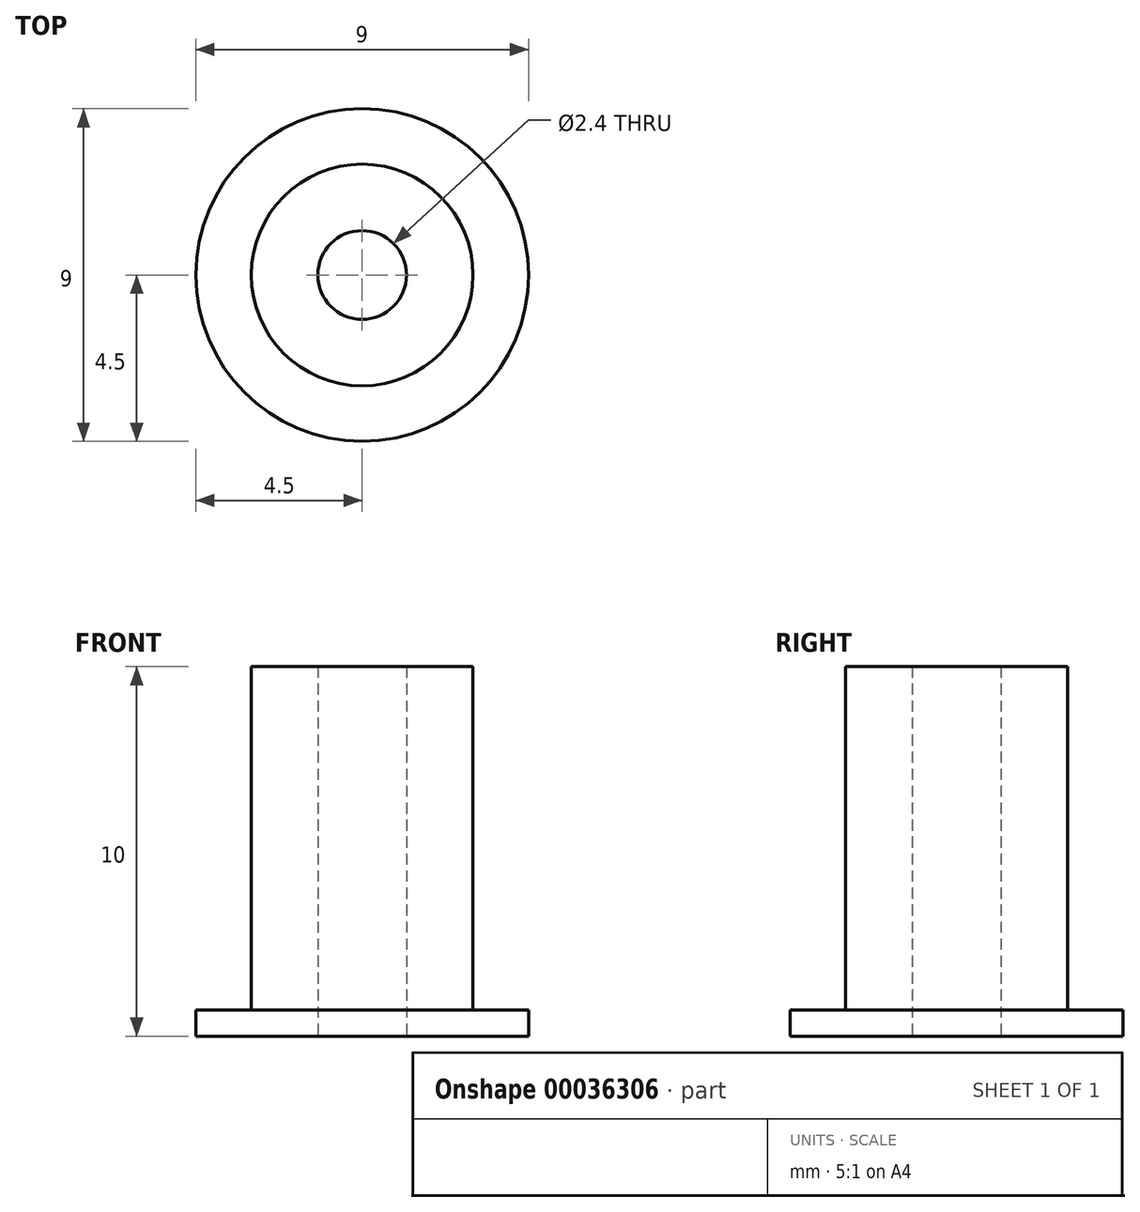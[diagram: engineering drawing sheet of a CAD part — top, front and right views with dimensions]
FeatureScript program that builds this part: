
annotation { "Feature Type Name" : "Feature", "Feature Type Description" : "" }
export const myFeature = defineFeature(function(context is Context, id is Id, definition is map)
    precondition{}
    {
        {
            var Q0;
            Q0=qCreatedBy(makeId("Top.planeOp"),FACE);
            var sketch = newSketch(context, id + "F0", { "sketchPlane" : qUnion([Q0])});
            skCircle(sketch, "E0", {"center": v(0, 0) * mm, "radius": 3 * mm});
            skCircle(sketch, "E1", {"center": v(0, 0) * mm, "radius": 4.5 * mm});
            skCircle(sketch, "E2", {"center": v(0, 0) * mm, "radius": 1.2 * mm});
            skSolve(sketch);
        }
        {
            var Q0;
            Q0=makeQuery(id+"F0.imprint","IMPRINT",FACE,{"disambiguationData":[TD([[makeQuery(id+"F0.imprint","IMPRINT",EDGE,{"derivedFrom":sQuery(id+"F0.wireOp",EDGE,"E0")}),-1.0]])]});
            var Q1;
            Q1=makeQuery(id+"F0.imprint","IMPRINT",FACE,{"disambiguationData":[TD([[makeQuery(id+"F0.imprint","IMPRINT",EDGE,{"derivedFrom":sQuery(id+"F0.wireOp",EDGE,"E0")}),1.0]])]});
            extrude(context, id + "F1", {"entities" : qUnion([Q0, Q1]), "depth" : 0.7 * mm});
        }
        {
            var Q0;
            Q0=makeQuery(id+"F0.imprint","IMPRINT",FACE,{"disambiguationData":[TD([[makeQuery(id+"F0.imprint","IMPRINT",EDGE,{"derivedFrom":sQuery(id+"F0.wireOp",EDGE,"E0")}),1.0]])]});
            extrude(context, id + "F2", {"entities" : qUnion([Q0]), "operationType" : NewBodyOperationType.ADD, "depth" : 10 * mm});
        }
    });
